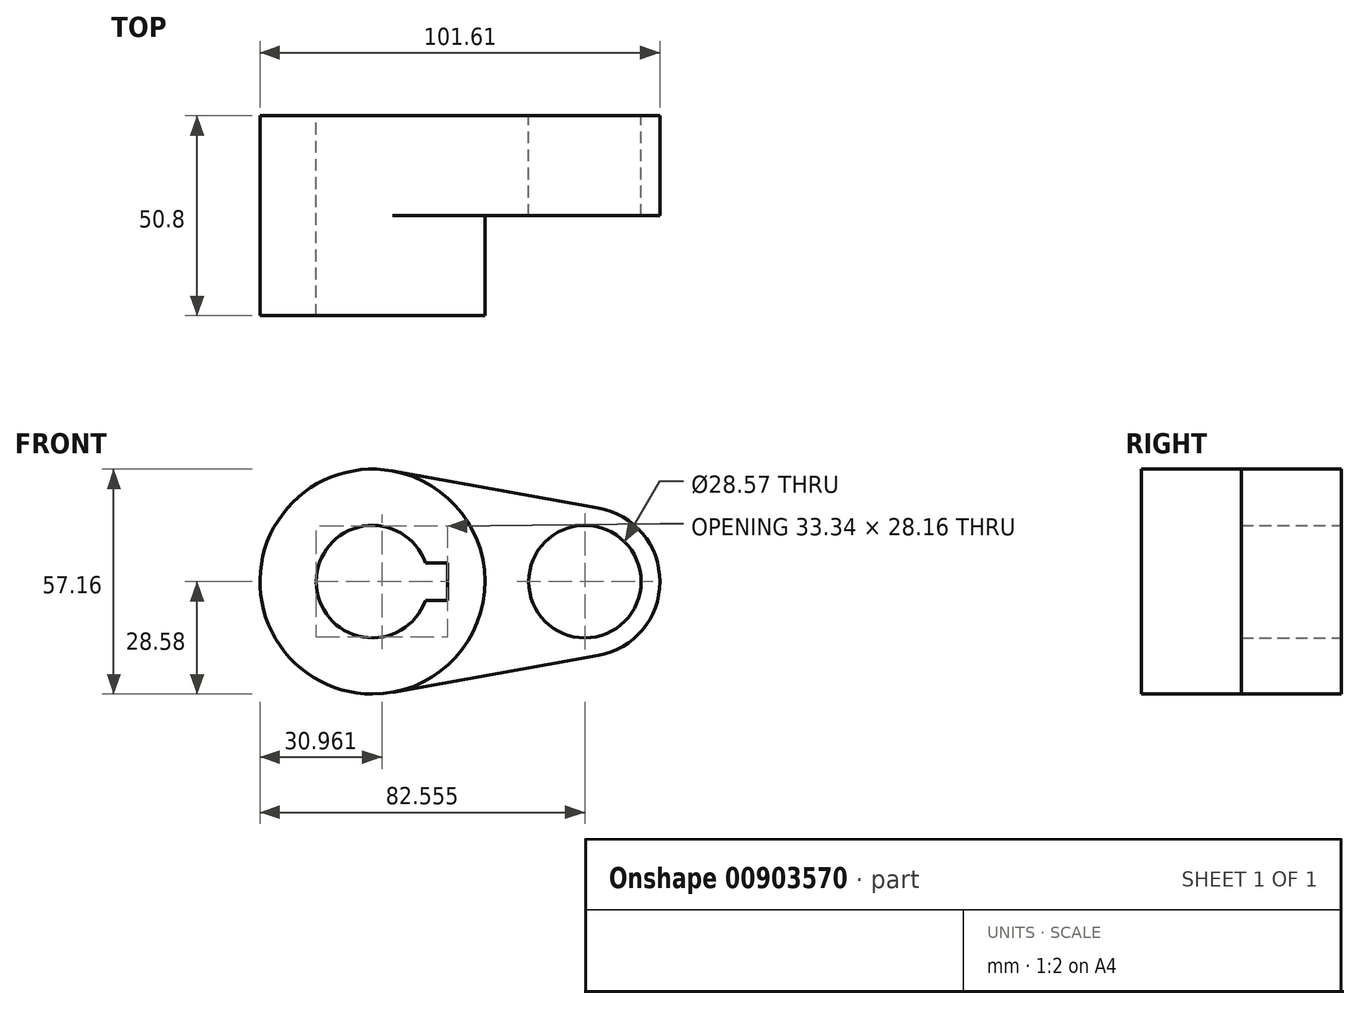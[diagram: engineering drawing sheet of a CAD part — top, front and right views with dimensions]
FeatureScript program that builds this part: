
annotation { "Feature Type Name" : "Feature", "Feature Type Description" : "" }
export const myFeature = defineFeature(function(context is Context, id is Id, definition is map)
    precondition{}
    {
        {
            var Q0;
            Q0=qCreatedBy(makeId("Front.planeOp"),FACE);
            var sketch = newSketch(context, id + "F0", { "sketchPlane" : qUnion([Q0])});
            skCircle(sketch, "E0", {"center": v(0, 0) * mm, "radius": 28.57 * mm});
            skCircle(sketch, "E1", {"center": v(53.98, 0) * mm, "radius": 19.05 * mm});
            skLineSegment(sketch, "E2", {"start": v(5.04, 28.13) * mm, "end": v(57.34, 18.75) * mm});
            skLineSegment(sketch, "E3", {"start": v(5.04, -28.13) * mm, "end": v(57.34, -18.75) * mm});
            skCircle(sketch, "E4", {"center": v(0, 0) * mm, "radius": 14.29 * mm});
            skCircle(sketch, "E5", {"center": v(53.98, 0) * mm, "radius": 14.29 * mm});
            skLineSegment(sketch, "E6.bottom", {"start": v(19.05, -4.76) * mm, "end": v(-19.05, -4.76) * mm});
            skLineSegment(sketch, "E6.top", {"start": v(19.05, 4.76) * mm, "end": v(-19.05, 4.76) * mm});
            skLineSegment(sketch, "E6.left", {"start": v(19.05, -4.76) * mm, "end": v(19.05, 4.76) * mm});
            skLineSegment(sketch, "E6.right", {"start": v(-19.05, -4.76) * mm, "end": v(-19.05, 4.76) * mm});
            skSolve(sketch);
        }
        {
            var Q0;
            {var subQ0=sQuery(id+"F0.wireOp",EDGE,"E2");Q0=makeQuery(id+"F0.imprint","IMPRINT",FACE,{"disambiguationData":[TD([[makeQuery(id+"F0.imprint","IMPRINT",EDGE,{"derivedFrom":subQ0}),-1.0]])]});}
            var Q1;
            Q1=makeQuery(id+"F0.imprint","IMPRINT",FACE,{"disambiguationData":[TD([[makeQuery(id+"F0.imprint","IMPRINT",EDGE,{"derivedFrom":sQuery(id+"F0.wireOp",EDGE,"E5")}),-1.0]])]});
            var Q2;
            {var subQ7=sQuery(id+"F0.wireOp",EDGE,"E6.left");Q2=makeQuery(id+"F0.imprint","IMPRINT",FACE,{"disambiguationData":[TD([[makeQuery(id+"F0.imprint","IMPRINT",EDGE,{"derivedFrom":subQ7}),-1.0]])]});}
            var Q3;
            {var subQ5=sQuery(id+"F0.wireOp",EDGE,"E6.right");Q3=makeQuery(id+"F0.imprint","IMPRINT",FACE,{"disambiguationData":[TD([[makeQuery(id+"F0.imprint","IMPRINT",EDGE,{"derivedFrom":subQ5}),-1.0]])]});}
            extrude(context, id + "F1", {"entities" : qUnion([Q0, Q1, Q2, Q3]), "depth" : 25.4 * mm, "offsetDistance" : 25.4 * mm});
        }
        {
            var Q0;
            {var subQ7=sQuery(id+"F0.wireOp",EDGE,"E6.left");Q0=makeQuery(id+"F0.imprint","IMPRINT",FACE,{"disambiguationData":[TD([[makeQuery(id+"F0.imprint","IMPRINT",EDGE,{"derivedFrom":subQ7}),-1.0]])]});}
            var Q1;
            {var subQ5=sQuery(id+"F0.wireOp",EDGE,"E6.right");Q1=makeQuery(id+"F0.imprint","IMPRINT",FACE,{"disambiguationData":[TD([[makeQuery(id+"F0.imprint","IMPRINT",EDGE,{"derivedFrom":subQ5}),-1.0]])]});}
            extrude(context, id + "F2", {"entities" : qUnion([Q0, Q1]), "operationType" : NewBodyOperationType.ADD, "depth" : 50.8 * mm, "offsetDistance" : 25.4 * mm});
        }
    });
